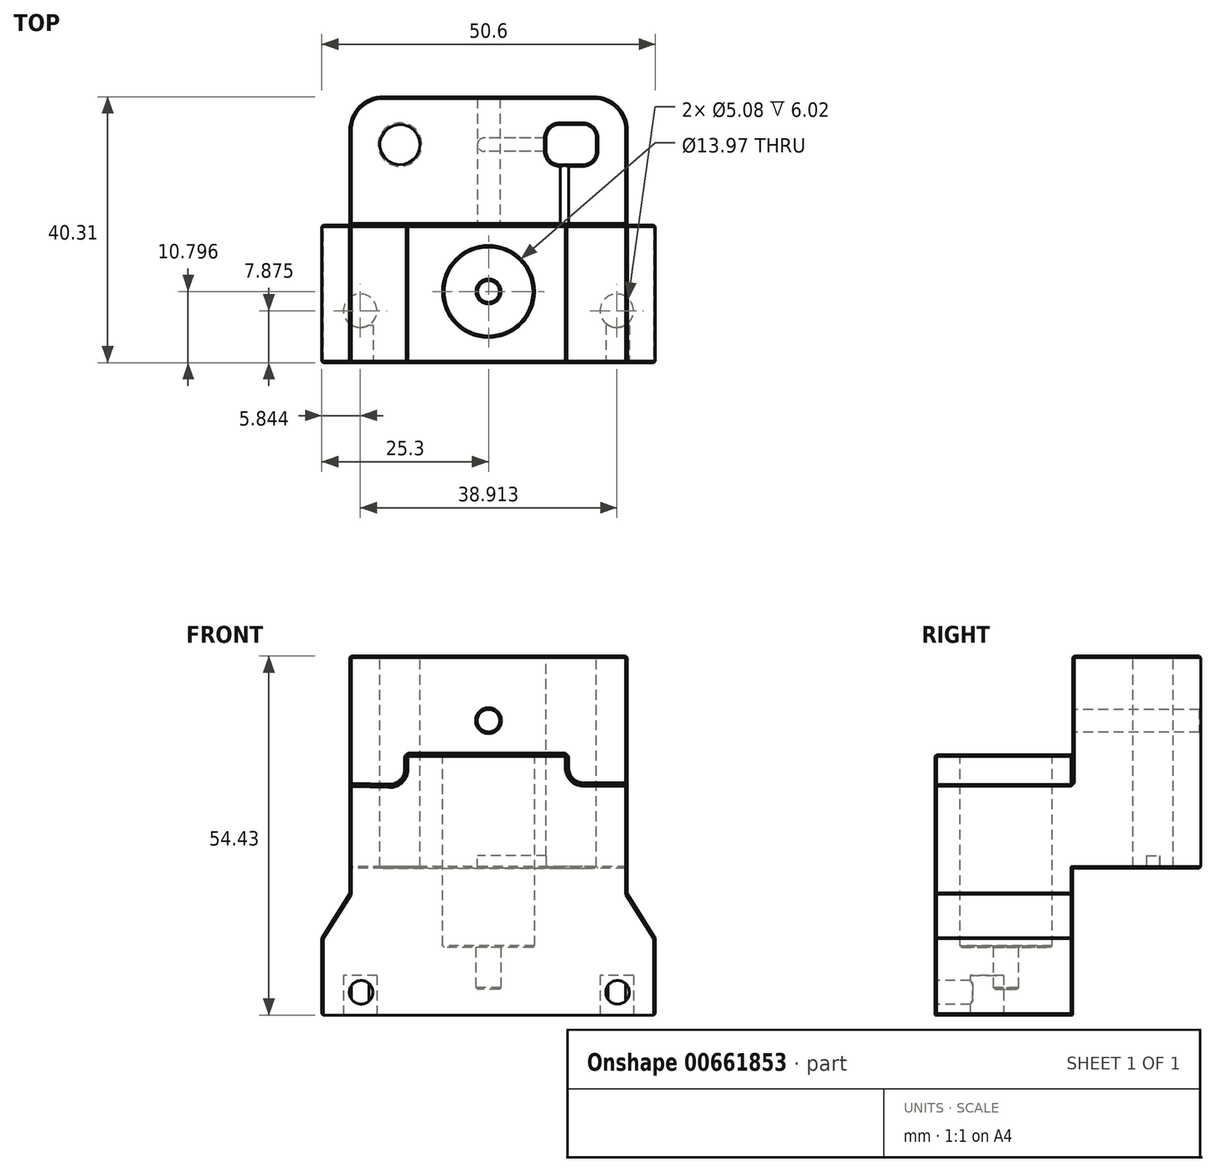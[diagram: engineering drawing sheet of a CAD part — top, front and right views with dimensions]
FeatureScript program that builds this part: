
annotation { "Feature Type Name" : "Feature", "Feature Type Description" : "" }
export const myFeature = defineFeature(function(context is Context, id is Id, definition is map)
    precondition{}
    {
        {
            var Q0;
            Q0=qCreatedBy(makeId("Front.planeOp"),FACE);
            var sketch = newSketch(context, id + "F0", { "sketchPlane" : qUnion([Q0])});
            skLineSegment(sketch, "E0.top", {"start": v(-25.3, -19.99) * mm, "end": v(25.3, -19.99) * mm});
            skPoint(sketch, "E1", {"position": v(-12.47, 14.68) * mm});
            skPoint(sketch, "E2", {"position": v(11.9, 14.96) * mm});
            skPoint(sketch, "E3", {"position": v(-25.3, -8.3) * mm});
            skPoint(sketch, "E4", {"position": v(-21.06, -1.57) * mm});
            skPoint(sketch, "E5", {"position": v(21.06, -1.57) * mm});
            skPoint(sketch, "E6", {"position": v(25.3, -8.3) * mm});
            skLineSegment(sketch, "E7", {"start": v(-25.3, -8.3) * mm, "end": v(-21.06, -1.57) * mm});
            skLineSegment(sketch, "E8", {"start": v(-21.06, -1.57) * mm, "end": v(-21.06, 14.94) * mm});
            skLineSegment(sketch, "E9", {"start": v(-21.06, 14.94) * mm, "end": v(-12.47, 14.68) * mm});
            skLineSegment(sketch, "E10", {"start": v(-12.47, 14.68) * mm, "end": v(-12.47, 19.48) * mm});
            skLineSegment(sketch, "E11", {"start": v(-12.47, 19.48) * mm, "end": v(11.9, 19.48) * mm});
            skLineSegment(sketch, "E12", {"start": v(11.9, 19.48) * mm, "end": v(11.9, 14.96) * mm});
            skLineSegment(sketch, "E13", {"start": v(21.06, 14.96) * mm, "end": v(11.9, 14.96) * mm});
            skLineSegment(sketch, "E14", {"start": v(21.06, 14.96) * mm, "end": v(21.06, -1.57) * mm});
            skLineSegment(sketch, "E15", {"start": v(21.06, -1.57) * mm, "end": v(25.3, -8.3) * mm});
            skLineSegment(sketch, "E16", {"start": v(25.3, -19.99) * mm, "end": v(25.3, -8.3) * mm});
            skLineSegment(sketch, "E17", {"start": v(25.3, -19.99) * mm, "end": v(-25.3, -19.99) * mm});
            skLineSegment(sketch, "E18", {"start": v(-25.3, -19.99) * mm, "end": v(-25.3, -8.3) * mm});
            skSolve(sketch);
        }
        {
            var Q0;
            Q0=makeQuery(id+"F0.imprint","IMPRINT",FACE,{"disambiguationData":[TD([[makeQuery(id+"F0.imprint","IMPRINT",EDGE,{"derivedFrom":sQuery(id+"F0.wireOp",EDGE,"E7")}),-1.0]])]});
            extrude(context, id + "F1", {"entities" : qUnion([Q0]), "depth" : 20.88 * mm, "offsetDistance" : 25.4 * mm});
        }
        {
            var Q0;
            Q0=makeQuery(id+"F1.opExtrude","CAP_FACE",FACE,{"disambiguationData":[OSD([sQuery(id+"F0.wireOp",EDGE,"E7"),sQuery(id+"F0.wireOp",EDGE,"E8"),sQuery(id+"F0.wireOp",EDGE,"E9"),sQuery(id+"F0.wireOp",EDGE,"E10"),sQuery(id+"F0.wireOp",EDGE,"E11"),sQuery(id+"F0.wireOp",EDGE,"E12"),sQuery(id+"F0.wireOp",EDGE,"E13"),sQuery(id+"F0.wireOp",EDGE,"E14"),sQuery(id+"F0.wireOp",EDGE,"E15"),sQuery(id+"F0.wireOp",EDGE,"E16"),sQuery(id+"F0.wireOp",EDGE,"E17"),sQuery(id+"F0.wireOp",EDGE,"E18")])],"isStart":true});
            var sketch = newSketch(context, id + "F2", { "sketchPlane" : qUnion([Q0])});
            skLineSegment(sketch, "E19", {"start": v(-21.06, 2.26) * mm, "end": v(-21.06, 34.44) * mm});
            skLineSegment(sketch, "E20", {"start": v(21.06, 2.26) * mm, "end": v(21.06, 34.44) * mm});
            skLineSegment(sketch, "E21", {"start": v(21.06, 34.44) * mm, "end": v(-21.06, 34.44) * mm});
            skLineSegment(sketch, "E22", {"start": v(-21.06, 2.26) * mm, "end": v(21.06, 2.26) * mm});
            skCircle(sketch, "E23", {"center": v(0, 24.65) * mm, "radius": 1.71 * mm});
            skSolve(sketch);
        }
        {
            var Q0;
            {var subQ0=sQuery(id+"F2.wireOp",EDGE,"E21");Q0=makeQuery(id+"F2.imprint","IMPRINT",FACE,{"disambiguationData":[TD([[makeQuery(id+"F2.imprint","IMPRINT",EDGE,{"derivedFrom":subQ0}),1.0]])]});}
            var Q1;
            {var subQ2=sQuery(id+"F2.wireOp",EDGE,"E22");Q1=makeQuery(id+"F2.imprint","IMPRINT",FACE,{"disambiguationData":[TD([[makeQuery(id+"F2.imprint","IMPRINT",EDGE,{"derivedFrom":subQ2}),1.0]])]});}
            extrude(context, id + "F3", {"entities" : qUnion([Q0, Q1]), "operationType" : NewBodyOperationType.ADD, "depth" : 19.43 * mm, "offsetDistance" : 25.4 * mm});
        }
        {
            var Q0;
            Q0=makeQuery(id+"F3.opExtrude","CAP_FACE",FACE,{"disambiguationData":[OSD([sQuery(id+"F2.wireOp",EDGE,"E19"),sQuery(id+"F2.wireOp",EDGE,"E20"),sQuery(id+"F2.wireOp",EDGE,"E21"),sQuery(id+"F2.wireOp",EDGE,"E22"),sQuery(id+"F2.wireOp",EDGE,"E23")])],"isStart":true});
            var sketch = newSketch(context, id + "F4", { "sketchPlane" : qUnion([Q0])});
            skPoint(sketch, "E24", {"position": v(12.17, 34.44) * mm});
            skPoint(sketch, "E25", {"position": v(10.9, 34.44) * mm});
            skArc(sketch, "E26", {"start": v(10.9, 34.44) * mm, "mid": v(11.53, 34.35) * mm, "end": v(12.17, 34.44) * mm});
            skSolve(sketch);
        }
        {
            var Q0;
            Q0=qCreatedBy(makeId("Front.planeOp"),FACE);
            cPlane(context, id + "F5", {"entities" : qUnion([Q0]), "cplaneType" : CPlaneType.OFFSET, "offset" : 20.88 * mm, "width" : 152.4 * mm, "height" : 152.4 * mm});
        }
        {
            var Q0;
            Q0=qCreatedBy(makeId("Top.planeOp"),FACE);
            cPlane(context, id + "F6", {"entities" : qUnion([Q0]), "cplaneType" : CPlaneType.OFFSET, "offset" : 34.44 * mm, "width" : 152.4 * mm, "height" : 152.4 * mm});
        }
        {
            var Q0;
            Q0=makeQuery(id+"F1.opExtrude","SWEPT_EDGE",EDGE,{"disambiguationData":[OSD([sQuery(id+"F0.wireOp",EDGE,"E12"),sQuery(id+"F0.wireOp",EDGE,"E13")])]});
            var Q1;
            Q1=makeQuery(id+"F1.opExtrude","SWEPT_EDGE",EDGE,{"disambiguationData":[OSD([sQuery(id+"F0.wireOp",EDGE,"E9"),sQuery(id+"F0.wireOp",EDGE,"E10")])]});
            fillet(context, id + "F7", {"entities" : qUnion([Q0, Q1]), "radius" : 2.54 * mm, "tangentPropagation" : true, "allowEdgeOverflow" : false});
        }
        {
            var Q0;
            Q0=makeQuery(id+"F3.opExtrude","CAP_EDGE",EDGE,{"disambiguationData":[OSD([sQuery(id+"F2.wireOp",EDGE,"E19")])],"isStart":false});
            var Q1;
            Q1=makeQuery(id+"F3.opExtrude","CAP_EDGE",EDGE,{"disambiguationData":[OSD([sQuery(id+"F2.wireOp",EDGE,"E20")])],"isStart":false});
            fillet(context, id + "F8", {"entities" : qUnion([Q0, Q1]), "radius" : 5.08 * mm, "tangentPropagation" : true, "allowEdgeOverflow" : false});
        }
        {
            var Q0;
            Q0=qCreatedBy(makeId("Top.planeOp"),FACE);
            cPlane(context, id + "F9", {"entities" : qUnion([Q0]), "cplaneType" : CPlaneType.OFFSET, "offset" : 19.48 * mm, "width" : 152.4 * mm, "height" : 152.4 * mm});
        }
        {
            var Q0;
            Q0=qCreatedBy(id+"F9.planeOp",FACE);
            var sketch = newSketch(context, id + "F10", { "sketchPlane" : qUnion([Q0])});
            skCircle(sketch, "E27", {"center": v(0, -10.08) * mm, "radius": 6.99 * mm});
            skCircle(sketch, "E28", {"center": v(0, -10.08) * mm, "radius": 1.9 * mm});
            skSolve(sketch);
        }
        {
            var Q0;
            Q0 = qSketchRegion(id + "F10", true);
            extrude(context, id + "F11", {"entities" : qUnion([Q0]), "operationType" : NewBodyOperationType.REMOVE, "oppositeDirection" : true, "depth" : 29.2 * mm, "offsetDistance" : 25.4 * mm});
        }
        {
            var Q0;
            Q0=makeQuery(id+"F11.boolean.opBoolean","SPLIT",FACE,{"disambiguationData":[TD([makeQuery(id+"F11.opExtrude","SWEPT_FACE",FACE,{"disambiguationData":[OSD([sQuery(id+"F10.wireOp",EDGE,"E28")])]})])],"derivedFrom":makeQuery(id+"F1.opExtrude","SWEPT_FACE",FACE,{"disambiguationData":[OSD([sQuery(id+"F0.wireOp",EDGE,"E11")])]})});
            extrude(context, id + "F12", {"entities" : qUnion([Q0]), "operationType" : NewBodyOperationType.REMOVE, "oppositeDirection" : true, "depth" : 35.56 * mm, "offsetDistance" : 25.4 * mm});
        }
        {
            var Q0;
            Q0=qCreatedBy(id+"F6.planeOp",FACE);
            var sketch = newSketch(context, id + "F13", { "sketchPlane" : qUnion([Q0])});
            skCircle(sketch, "E29", {"center": v(-13.44, 12.2) * mm, "radius": 3.05 * mm});
            skLineSegment(sketch, "E30.bottom", {"start": v(16.36, 9.14) * mm, "end": v(8.74, 9.14) * mm});
            skLineSegment(sketch, "E30.top", {"start": v(16.36, 15.24) * mm, "end": v(8.74, 15.24) * mm});
            skLineSegment(sketch, "E30.left", {"start": v(16.36, 9.14) * mm, "end": v(16.36, 15.24) * mm});
            skLineSegment(sketch, "E30.right", {"start": v(8.74, 9.14) * mm, "end": v(8.74, 15.24) * mm});
            skSolve(sketch);
        }
        {
            var Q0;
            Q0 = qSketchRegion(id + "F13", true);
            extrude(context, id + "F14", {"entities" : qUnion([Q0]), "operationType" : NewBodyOperationType.REMOVE, "endBound" : BoundingType.THROUGH_ALL, "oppositeDirection" : true, "depth" : 25.4 * mm, "offsetDistance" : 25.4 * mm});
        }
        {
            var Q0;
            Q0=makeQuery(id+"F14.boolean.opBoolean","COPY",EDGE,{"derivedFrom":makeQuery(id+"F14.opExtrude","SWEPT_EDGE",EDGE,{"disambiguationData":[OSD([sQuery(id+"F13.wireOp",EDGE,"E30.bottom"),sQuery(id+"F13.wireOp",EDGE,"E30.left")])]})});
            var Q1;
            Q1=makeQuery(id+"F14.boolean.opBoolean","COPY",EDGE,{"derivedFrom":makeQuery(id+"F14.opExtrude","SWEPT_EDGE",EDGE,{"disambiguationData":[OSD([sQuery(id+"F13.wireOp",EDGE,"E30.top"),sQuery(id+"F13.wireOp",EDGE,"E30.right")])]})});
            var Q2;
            Q2=makeQuery(id+"F14.boolean.opBoolean","COPY",EDGE,{"derivedFrom":makeQuery(id+"F14.opExtrude","SWEPT_EDGE",EDGE,{"disambiguationData":[OSD([sQuery(id+"F13.wireOp",EDGE,"E30.bottom"),sQuery(id+"F13.wireOp",EDGE,"E30.right")])]})});
            var Q3;
            Q3=makeQuery(id+"F14.boolean.opBoolean","COPY",EDGE,{"derivedFrom":makeQuery(id+"F14.opExtrude","SWEPT_EDGE",EDGE,{"disambiguationData":[OSD([sQuery(id+"F13.wireOp",EDGE,"E30.top"),sQuery(id+"F13.wireOp",EDGE,"E30.left")])]})});
            fillet(context, id + "F15", {"entities" : qUnion([Q0, Q1, Q2, Q3]), "radius" : 2.03 * mm, "tangentPropagation" : true, "allowEdgeOverflow" : false});
        }
        {
            var Q0;
            Q0=makeQuery(id+"F8.opFillet","BLEND_EDGE",EDGE,{"blendedFrom":[makeQuery(id+"F3.opExtrude","CAP_EDGE",EDGE,{"disambiguationData":[OSD([sQuery(id+"F2.wireOp",EDGE,"E19")])],"isStart":false}),makeQuery(id+"F3.opExtrude","SWEPT_FACE",FACE,{"disambiguationData":[OSD([sQuery(id+"F2.wireOp",EDGE,"E22")])]})],"blendedInto":[makeQuery(id+"F3.opExtrude","SWEPT_FACE",FACE,{"disambiguationData":[OSD([sQuery(id+"F2.wireOp",EDGE,"E22")])]})]});
            var Q1;
            Q1=makeQuery(id+"F1.opExtrude","SWEPT_EDGE",EDGE,{"disambiguationData":[OSD([sQuery(id+"F0.wireOp",EDGE,"E7"),sQuery(id+"F0.wireOp",EDGE,"E18")])]});
            var Q2;
            {var subQ0=sQuery(id+"F2.wireOp",EDGE,"E19");Q2=makeQuery(id+"F8.opFillet","BLEND_EDGE",EDGE,{"blendedFrom":[makeQuery(id+"F3.opExtrude","CAP_EDGE",EDGE,{"disambiguationData":[OSD([subQ0])],"isStart":false}),makeQuery(id+"F3.opExtrude","CAP_FACE",FACE,{"disambiguationData":[OSD([subQ0,sQuery(id+"F2.wireOp",EDGE,"E20"),sQuery(id+"F2.wireOp",EDGE,"E21"),sQuery(id+"F2.wireOp",EDGE,"E22"),sQuery(id+"F2.wireOp",EDGE,"E23")])],"isStart":false})],"blendedInto":[makeQuery(id+"F3.opExtrude","CAP_FACE",FACE,{"disambiguationData":[OSD([subQ0,sQuery(id+"F2.wireOp",EDGE,"E20"),sQuery(id+"F2.wireOp",EDGE,"E21"),sQuery(id+"F2.wireOp",EDGE,"E22"),sQuery(id+"F2.wireOp",EDGE,"E23")])],"isStart":false})]});}
            var Q3;
            Q3=makeQuery(id+"F8.opFillet","BLEND_EDGE",EDGE,{"blendedFrom":[makeQuery(id+"F3.opExtrude","CAP_EDGE",EDGE,{"disambiguationData":[OSD([sQuery(id+"F2.wireOp",EDGE,"E20")])],"isStart":false}),makeQuery(id+"F3.opExtrude","SWEPT_FACE",FACE,{"disambiguationData":[OSD([sQuery(id+"F2.wireOp",EDGE,"E21")])]})],"blendedInto":[makeQuery(id+"F3.opExtrude","SWEPT_FACE",FACE,{"disambiguationData":[OSD([sQuery(id+"F2.wireOp",EDGE,"E21")])]})]});
            var Q4;
            Q4=makeQuery(id+"F8.opFillet","BLEND_EDGE",EDGE,{"blendedFrom":[makeQuery(id+"F3.opExtrude","CAP_EDGE",EDGE,{"disambiguationData":[OSD([sQuery(id+"F2.wireOp",EDGE,"E19")])],"isStart":false}),makeQuery(id+"F3.opExtrude","SWEPT_FACE",FACE,{"disambiguationData":[OSD([sQuery(id+"F2.wireOp",EDGE,"E21")])]})],"blendedInto":[makeQuery(id+"F3.opExtrude","SWEPT_FACE",FACE,{"disambiguationData":[OSD([sQuery(id+"F2.wireOp",EDGE,"E21")])]})]});
            var Q5;
            Q5=makeQuery(id+"F3.opExtrude","CAP_EDGE",EDGE,{"disambiguationData":[OSD([sQuery(id+"F2.wireOp",EDGE,"E22")])],"isStart":false});
            var Q6;
            Q6=makeQuery(id+"F1.opExtrude","SWEPT_EDGE",EDGE,{"disambiguationData":[OSD([sQuery(id+"F0.wireOp",EDGE,"E17"),sQuery(id+"F0.wireOp",EDGE,"E18")])]});
            var Q7;
            Q7=makeQuery(id+"F1.opExtrude","SWEPT_EDGE",EDGE,{"disambiguationData":[OSD([sQuery(id+"F0.wireOp",EDGE,"E8"),sQuery(id+"F0.wireOp",EDGE,"E9")])]});
            var Q8;
            Q8=makeQuery(id+"F1.opExtrude","SWEPT_EDGE",EDGE,{"disambiguationData":[OSD([sQuery(id+"F0.wireOp",EDGE,"E16"),sQuery(id+"F0.wireOp",EDGE,"E17")])]});
            var Q9;
            Q9=makeQuery(id+"F3.opExtrude","SWEPT_EDGE",EDGE,{"disambiguationData":[OSD([sQuery(id+"F0.wireOp",EDGE,"E8"),sQuery(id+"F2.wireOp",EDGE,"E20"),sQuery(id+"F2.wireOp",EDGE,"E22")])]});
            var Q10;
            Q10=makeQuery(id+"F1.opExtrude","CAP_EDGE",EDGE,{"disambiguationData":[OSD([sQuery(id+"F0.wireOp",EDGE,"E7")])],"isStart":true});
            var Q11;
            Q11=makeQuery(id+"F3.opExtrude","SWEPT_EDGE",EDGE,{"disambiguationData":[OSD([sQuery(id+"F0.wireOp",EDGE,"E14"),sQuery(id+"F2.wireOp",EDGE,"E19"),sQuery(id+"F2.wireOp",EDGE,"E22")])]});
            var Q12;
            Q12=makeQuery(id+"F1.opExtrude","CAP_EDGE",EDGE,{"disambiguationData":[OSD([sQuery(id+"F0.wireOp",EDGE,"E14")])],"isStart":true});
            var Q13;
            Q13=makeQuery(id+"F1.opExtrude","CAP_EDGE",EDGE,{"disambiguationData":[OSD([sQuery(id+"F0.wireOp",EDGE,"E17")])],"isStart":false});
            var Q14;
            Q14=makeQuery(id+"F1.opExtrude","CAP_EDGE",EDGE,{"disambiguationData":[OSD([sQuery(id+"F0.wireOp",EDGE,"E18")])],"isStart":false});
            var Q15;
            Q15=makeQuery(id+"F1.opExtrude","CAP_EDGE",EDGE,{"disambiguationData":[OSD([sQuery(id+"F0.wireOp",EDGE,"E8")])],"isStart":true});
            var Q16;
            Q16=makeQuery(id+"F3.opExtrude","CAP_EDGE",EDGE,{"disambiguationData":[OSD([sQuery(id+"F2.wireOp",EDGE,"E23")])],"isStart":false});
            var Q17;
            Q17=makeQuery(id+"F15.opFillet","BLEND_EDGE",EDGE,{"blendedFrom":[makeQuery(id+"F14.boolean.opBoolean","COPY",EDGE,{"derivedFrom":makeQuery(id+"F14.opExtrude","SWEPT_EDGE",EDGE,{"disambiguationData":[OSD([sQuery(id+"F13.wireOp",EDGE,"E30.top"),sQuery(id+"F13.wireOp",EDGE,"E30.left")])]})}),makeQuery(id+"F3.opExtrude","SWEPT_FACE",FACE,{"disambiguationData":[OSD([sQuery(id+"F2.wireOp",EDGE,"E22")])]})],"blendedInto":[makeQuery(id+"F3.opExtrude","SWEPT_FACE",FACE,{"disambiguationData":[OSD([sQuery(id+"F2.wireOp",EDGE,"E22")])]})]});
            var Q18;
            Q18=makeQuery(id+"F14.boolean.opBoolean","INTERSECT",EDGE,{"derivedFrom":[makeQuery(id+"F3.opExtrude","SWEPT_FACE",FACE,{"disambiguationData":[OSD([sQuery(id+"F2.wireOp",EDGE,"E22")])]}),makeQuery(id+"F14.opExtrude","SWEPT_FACE",FACE,{"disambiguationData":[OSD([sQuery(id+"F13.wireOp",EDGE,"E29")])]})]});
            var Q19;
            Q19=makeQuery(id+"F15.opFillet","BLEND_EDGE",EDGE,{"blendedFrom":[makeQuery(id+"F14.boolean.opBoolean","COPY",EDGE,{"derivedFrom":makeQuery(id+"F14.opExtrude","SWEPT_EDGE",EDGE,{"disambiguationData":[OSD([sQuery(id+"F13.wireOp",EDGE,"E30.top"),sQuery(id+"F13.wireOp",EDGE,"E30.right")])]})}),makeQuery(id+"F3.opExtrude","SWEPT_FACE",FACE,{"disambiguationData":[OSD([sQuery(id+"F2.wireOp",EDGE,"E22")])]})],"blendedInto":[makeQuery(id+"F3.opExtrude","SWEPT_FACE",FACE,{"disambiguationData":[OSD([sQuery(id+"F2.wireOp",EDGE,"E22")])]})]});
            var Q20;
            Q20=makeQuery(id+"F3.opExtrude","CAP_EDGE",EDGE,{"disambiguationData":[OSD([sQuery(id+"F2.wireOp",EDGE,"E21")])],"isStart":false});
            var Q21;
            Q21=makeQuery(id+"F8.opFillet","BLEND_EDGE",EDGE,{"blendedFrom":[makeQuery(id+"F3.opExtrude","CAP_EDGE",EDGE,{"disambiguationData":[OSD([sQuery(id+"F2.wireOp",EDGE,"E20")])],"isStart":false}),makeQuery(id+"F3.opExtrude","SWEPT_FACE",FACE,{"disambiguationData":[OSD([sQuery(id+"F2.wireOp",EDGE,"E22")])]})],"blendedInto":[makeQuery(id+"F3.opExtrude","SWEPT_FACE",FACE,{"disambiguationData":[OSD([sQuery(id+"F2.wireOp",EDGE,"E22")])]})]});
            var Q22;
            {var subQ0=sQuery(id+"F2.wireOp",EDGE,"E20");Q22=makeQuery(id+"F8.opFillet","BLEND_EDGE",EDGE,{"blendedFrom":[makeQuery(id+"F3.opExtrude","CAP_EDGE",EDGE,{"disambiguationData":[OSD([subQ0])],"isStart":false}),makeQuery(id+"F3.boolean.opBoolean","MERGE",FACE,{"derivedFrom":[makeQuery(id+"F1.opExtrude","SWEPT_FACE",FACE,{"disambiguationData":[OSD([sQuery(id+"F0.wireOp",EDGE,"E8")])]}),makeQuery(id+"F3.opExtrude","SWEPT_FACE",FACE,{"disambiguationData":[OSD([subQ0])]})]})],"blendedInto":[makeQuery(id+"F3.boolean.opBoolean","MERGE",FACE,{"derivedFrom":[makeQuery(id+"F1.opExtrude","SWEPT_FACE",FACE,{"disambiguationData":[OSD([sQuery(id+"F0.wireOp",EDGE,"E8")])]}),makeQuery(id+"F3.opExtrude","SWEPT_FACE",FACE,{"disambiguationData":[OSD([subQ0])]})]})]});}
            var Q23;
            Q23=makeQuery(id+"F3.opExtrude","CAP_EDGE",EDGE,{"disambiguationData":[OSD([sQuery(id+"F2.wireOp",EDGE,"E20")])],"isStart":true});
            var Q24;
            Q24=makeQuery(id+"F1.opExtrude","SWEPT_EDGE",EDGE,{"disambiguationData":[OSD([sQuery(id+"F0.wireOp",EDGE,"E15"),sQuery(id+"F0.wireOp",EDGE,"E16")])]});
            var Q25;
            Q25=makeQuery(id+"F1.opExtrude","SWEPT_EDGE",EDGE,{"disambiguationData":[OSD([sQuery(id+"F0.wireOp",EDGE,"E7"),sQuery(id+"F0.wireOp",EDGE,"E8")])]});
            var Q26;
            Q26=makeQuery(id+"F1.opExtrude","CAP_EDGE",EDGE,{"disambiguationData":[OSD([sQuery(id+"F0.wireOp",EDGE,"E9")])],"isStart":true});
            var Q27;
            Q27=makeQuery(id+"F1.opExtrude","CAP_EDGE",EDGE,{"disambiguationData":[OSD([sQuery(id+"F0.wireOp",EDGE,"E11")])],"isStart":true});
            var Q28;
            Q28=makeQuery(id+"F1.opExtrude","CAP_EDGE",EDGE,{"disambiguationData":[OSD([sQuery(id+"F0.wireOp",EDGE,"E16")])],"isStart":false});
            var Q29;
            Q29=makeQuery(id+"F1.opExtrude","SWEPT_EDGE",EDGE,{"disambiguationData":[OSD([sQuery(id+"F0.wireOp",EDGE,"E13"),sQuery(id+"F0.wireOp",EDGE,"E14")])]});
            var Q30;
            Q30=makeQuery(id+"F1.opExtrude","CAP_EDGE",EDGE,{"disambiguationData":[OSD([sQuery(id+"F0.wireOp",EDGE,"E14")])],"isStart":false});
            var Q31;
            Q31=makeQuery(id+"F1.opExtrude","CAP_EDGE",EDGE,{"disambiguationData":[OSD([sQuery(id+"F0.wireOp",EDGE,"E7")])],"isStart":false});
            var Q32;
            Q32=makeQuery(id+"F3.opExtrude","SWEPT_EDGE",EDGE,{"disambiguationData":[OSD([sQuery(id+"F2.wireOp",EDGE,"E19"),sQuery(id+"F2.wireOp",EDGE,"E21")])]});
            var Q33;
            Q33=makeQuery(id+"F1.opExtrude","SWEPT_EDGE",EDGE,{"disambiguationData":[OSD([sQuery(id+"F0.wireOp",EDGE,"E14"),sQuery(id+"F0.wireOp",EDGE,"E15")])]});
            var Q34;
            {var subQ0=sQuery(id+"F0.wireOp",EDGE,"E13");Q34=makeQuery(id+"F7.opFillet","BLEND_EDGE",EDGE,{"blendedFrom":[makeQuery(id+"F1.opExtrude","SWEPT_EDGE",EDGE,{"disambiguationData":[OSD([sQuery(id+"F0.wireOp",EDGE,"E12"),subQ0])]}),makeQuery(id+"F1.opExtrude","SWEPT_FACE",FACE,{"disambiguationData":[OSD([subQ0])]})],"blendedInto":[makeQuery(id+"F1.opExtrude","SWEPT_FACE",FACE,{"disambiguationData":[OSD([subQ0])]})]});}
            var Q35;
            Q35=makeQuery(id+"F3.opExtrude","SWEPT_EDGE",EDGE,{"disambiguationData":[OSD([sQuery(id+"F2.wireOp",EDGE,"E20"),sQuery(id+"F2.wireOp",EDGE,"E21")])]});
            var Q36;
            Q36=makeQuery(id+"F1.opExtrude","CAP_EDGE",EDGE,{"disambiguationData":[OSD([sQuery(id+"F0.wireOp",EDGE,"E16")])],"isStart":true});
            var Q37;
            Q37=makeQuery(id+"F1.opExtrude","SWEPT_EDGE",EDGE,{"disambiguationData":[OSD([sQuery(id+"F0.wireOp",EDGE,"E11"),sQuery(id+"F0.wireOp",EDGE,"E12")])]});
            var Q38;
            Q38=makeQuery(id+"F1.opExtrude","CAP_EDGE",EDGE,{"disambiguationData":[OSD([sQuery(id+"F0.wireOp",EDGE,"E8")])],"isStart":false});
            var Q39;
            Q39=makeQuery(id+"F1.opExtrude","CAP_EDGE",EDGE,{"disambiguationData":[OSD([sQuery(id+"F0.wireOp",EDGE,"E11")])],"isStart":false});
            var Q40;
            Q40=makeQuery(id+"F1.opExtrude","CAP_EDGE",EDGE,{"disambiguationData":[OSD([sQuery(id+"F0.wireOp",EDGE,"E18")])],"isStart":true});
            var Q41;
            {var subQ0=sQuery(id+"F0.wireOp",EDGE,"E10");var subQ1=sQuery(id+"F0.wireOp",EDGE,"E9");Q41=makeQuery(id+"F7.opFillet","BLEND_EDGE",EDGE,{"blendedFrom":[makeQuery(id+"F1.opExtrude","SWEPT_EDGE",EDGE,{"disambiguationData":[OSD([subQ1,subQ0])]}),makeQuery(id+"F1.opExtrude","CAP_FACE",FACE,{"disambiguationData":[OSD([sQuery(id+"F0.wireOp",EDGE,"E7"),sQuery(id+"F0.wireOp",EDGE,"E8"),subQ1,subQ0,sQuery(id+"F0.wireOp",EDGE,"E11"),sQuery(id+"F0.wireOp",EDGE,"E12"),sQuery(id+"F0.wireOp",EDGE,"E13"),sQuery(id+"F0.wireOp",EDGE,"E14"),sQuery(id+"F0.wireOp",EDGE,"E15"),sQuery(id+"F0.wireOp",EDGE,"E16"),sQuery(id+"F0.wireOp",EDGE,"E17"),sQuery(id+"F0.wireOp",EDGE,"E18")])],"isStart":false})],"blendedInto":[makeQuery(id+"F1.opExtrude","CAP_FACE",FACE,{"disambiguationData":[OSD([sQuery(id+"F0.wireOp",EDGE,"E7"),sQuery(id+"F0.wireOp",EDGE,"E8"),subQ1,subQ0,sQuery(id+"F0.wireOp",EDGE,"E11"),sQuery(id+"F0.wireOp",EDGE,"E12"),sQuery(id+"F0.wireOp",EDGE,"E13"),sQuery(id+"F0.wireOp",EDGE,"E14"),sQuery(id+"F0.wireOp",EDGE,"E15"),sQuery(id+"F0.wireOp",EDGE,"E16"),sQuery(id+"F0.wireOp",EDGE,"E17"),sQuery(id+"F0.wireOp",EDGE,"E18")])],"isStart":false})]});}
            var Q42;
            Q42=makeQuery(id+"F1.opExtrude","CAP_EDGE",EDGE,{"disambiguationData":[OSD([sQuery(id+"F0.wireOp",EDGE,"E15")])],"isStart":false});
            var Q43;
            Q43=makeQuery(id+"F7.opFillet","BLEND_EDGE",EDGE,{"blendedFrom":[makeQuery(id+"F1.opExtrude","SWEPT_EDGE",EDGE,{"disambiguationData":[OSD([sQuery(id+"F0.wireOp",EDGE,"E9"),sQuery(id+"F0.wireOp",EDGE,"E10")])]}),makeQuery(id+"F3.opExtrude","CAP_FACE",FACE,{"disambiguationData":[OSD([sQuery(id+"F2.wireOp",EDGE,"E19"),sQuery(id+"F2.wireOp",EDGE,"E20"),sQuery(id+"F2.wireOp",EDGE,"E21"),sQuery(id+"F2.wireOp",EDGE,"E22"),sQuery(id+"F2.wireOp",EDGE,"E23")])],"isStart":true})],"blendedInto":[makeQuery(id+"F3.opExtrude","CAP_FACE",FACE,{"disambiguationData":[OSD([sQuery(id+"F2.wireOp",EDGE,"E19"),sQuery(id+"F2.wireOp",EDGE,"E20"),sQuery(id+"F2.wireOp",EDGE,"E21"),sQuery(id+"F2.wireOp",EDGE,"E22"),sQuery(id+"F2.wireOp",EDGE,"E23")])],"isStart":true})]});
            var Q44;
            Q44=makeQuery(id+"F1.opExtrude","CAP_EDGE",EDGE,{"disambiguationData":[OSD([sQuery(id+"F0.wireOp",EDGE,"E17")])],"isStart":true});
            var Q45;
            {var subQ0=sQuery(id+"F0.wireOp",EDGE,"E13");var subQ1=sQuery(id+"F0.wireOp",EDGE,"E12");Q45=makeQuery(id+"F7.opFillet","BLEND_EDGE",EDGE,{"blendedFrom":[makeQuery(id+"F1.opExtrude","SWEPT_EDGE",EDGE,{"disambiguationData":[OSD([subQ1,subQ0])]}),makeQuery(id+"F1.opExtrude","CAP_FACE",FACE,{"disambiguationData":[OSD([sQuery(id+"F0.wireOp",EDGE,"E7"),sQuery(id+"F0.wireOp",EDGE,"E8"),sQuery(id+"F0.wireOp",EDGE,"E9"),sQuery(id+"F0.wireOp",EDGE,"E10"),sQuery(id+"F0.wireOp",EDGE,"E11"),subQ1,subQ0,sQuery(id+"F0.wireOp",EDGE,"E14"),sQuery(id+"F0.wireOp",EDGE,"E15"),sQuery(id+"F0.wireOp",EDGE,"E16"),sQuery(id+"F0.wireOp",EDGE,"E17"),sQuery(id+"F0.wireOp",EDGE,"E18")])],"isStart":false})],"blendedInto":[makeQuery(id+"F1.opExtrude","CAP_FACE",FACE,{"disambiguationData":[OSD([sQuery(id+"F0.wireOp",EDGE,"E7"),sQuery(id+"F0.wireOp",EDGE,"E8"),sQuery(id+"F0.wireOp",EDGE,"E9"),sQuery(id+"F0.wireOp",EDGE,"E10"),sQuery(id+"F0.wireOp",EDGE,"E11"),subQ1,subQ0,sQuery(id+"F0.wireOp",EDGE,"E14"),sQuery(id+"F0.wireOp",EDGE,"E15"),sQuery(id+"F0.wireOp",EDGE,"E16"),sQuery(id+"F0.wireOp",EDGE,"E17"),sQuery(id+"F0.wireOp",EDGE,"E18")])],"isStart":false})]});}
            var Q46;
            Q46=makeQuery(id+"F12.boolean.opBoolean","COPY",EDGE,{"derivedFrom":makeQuery(id+"F12.opExtrude","CAP_EDGE",EDGE,{"disambiguationData":[OSD([sQuery(id+"F10.wireOp",EDGE,"E28")])],"isStart":false})});
            var Q47;
            Q47=makeQuery(id+"F3.opExtrude","CAP_EDGE",EDGE,{"disambiguationData":[OSD([sQuery(id+"F2.wireOp",EDGE,"E22")])],"isStart":true});
            var Q48;
            Q48=makeQuery(id+"F1.opExtrude","CAP_EDGE",EDGE,{"disambiguationData":[OSD([sQuery(id+"F0.wireOp",EDGE,"E15")])],"isStart":true});
            var Q49;
            Q49=makeQuery(id+"F3.opExtrude","CAP_EDGE",EDGE,{"disambiguationData":[OSD([sQuery(id+"F2.wireOp",EDGE,"E19")])],"isStart":true});
            var Q50;
            {var subQ0=sQuery(id+"F0.wireOp",EDGE,"E9");Q50=makeQuery(id+"F7.opFillet","BLEND_EDGE",EDGE,{"blendedFrom":[makeQuery(id+"F1.opExtrude","SWEPT_EDGE",EDGE,{"disambiguationData":[OSD([subQ0,sQuery(id+"F0.wireOp",EDGE,"E10")])]}),makeQuery(id+"F1.opExtrude","SWEPT_FACE",FACE,{"disambiguationData":[OSD([subQ0])]})],"blendedInto":[makeQuery(id+"F1.opExtrude","SWEPT_FACE",FACE,{"disambiguationData":[OSD([subQ0])]})]});}
            var Q51;
            Q51=makeQuery(id+"F14.boolean.opBoolean","INTERSECT",EDGE,{"derivedFrom":[makeQuery(id+"F3.opExtrude","SWEPT_FACE",FACE,{"disambiguationData":[OSD([sQuery(id+"F2.wireOp",EDGE,"E22")])]}),makeQuery(id+"F14.opExtrude","SWEPT_FACE",FACE,{"disambiguationData":[OSD([sQuery(id+"F13.wireOp",EDGE,"E30.top")])]})]});
            var Q52;
            Q52=makeQuery(id+"F14.boolean.opBoolean","INTERSECT",EDGE,{"derivedFrom":[makeQuery(id+"F3.opExtrude","SWEPT_FACE",FACE,{"disambiguationData":[OSD([sQuery(id+"F2.wireOp",EDGE,"E22")])]}),makeQuery(id+"F14.opExtrude","SWEPT_FACE",FACE,{"disambiguationData":[OSD([sQuery(id+"F13.wireOp",EDGE,"E30.bottom")])]})]});
            var Q53;
            Q53=makeQuery(id+"F14.boolean.opBoolean","COPY",EDGE,{"derivedFrom":makeQuery(id+"F14.opExtrude","CAP_EDGE",EDGE,{"disambiguationData":[OSD([sQuery(id+"F13.wireOp",EDGE,"E30.top")])],"isStart":true})});
            var Q54;
            Q54=makeQuery(id+"F14.boolean.opBoolean","COPY",EDGE,{"derivedFrom":makeQuery(id+"F14.opExtrude","CAP_EDGE",EDGE,{"disambiguationData":[OSD([sQuery(id+"F13.wireOp",EDGE,"E30.bottom")])],"isStart":true})});
            var Q55;
            {var subQ0=sQuery(id+"F13.wireOp",EDGE,"E30.top");Q55=makeQuery(id+"F15.opFillet","BLEND_EDGE",EDGE,{"blendedFrom":[makeQuery(id+"F14.boolean.opBoolean","COPY",EDGE,{"derivedFrom":makeQuery(id+"F14.opExtrude","SWEPT_EDGE",EDGE,{"disambiguationData":[OSD([subQ0,sQuery(id+"F13.wireOp",EDGE,"E30.right")])]})}),makeQuery(id+"F14.boolean.opBoolean","COPY",FACE,{"derivedFrom":makeQuery(id+"F14.opExtrude","SWEPT_FACE",FACE,{"disambiguationData":[OSD([subQ0])]})})],"blendedInto":[makeQuery(id+"F14.boolean.opBoolean","COPY",FACE,{"derivedFrom":makeQuery(id+"F14.opExtrude","SWEPT_FACE",FACE,{"disambiguationData":[OSD([subQ0])]})})]});}
            var Q56;
            Q56=makeQuery(id+"F15.opFillet","BLEND_EDGE",EDGE,{"blendedFrom":[makeQuery(id+"F14.boolean.opBoolean","COPY",EDGE,{"derivedFrom":makeQuery(id+"F14.opExtrude","SWEPT_EDGE",EDGE,{"disambiguationData":[OSD([sQuery(id+"F13.wireOp",EDGE,"E30.top"),sQuery(id+"F13.wireOp",EDGE,"E30.left")])]})}),makeQuery(id+"F3.opExtrude","SWEPT_FACE",FACE,{"disambiguationData":[OSD([sQuery(id+"F2.wireOp",EDGE,"E21")])]})],"blendedInto":[makeQuery(id+"F3.opExtrude","SWEPT_FACE",FACE,{"disambiguationData":[OSD([sQuery(id+"F2.wireOp",EDGE,"E21")])]})]});
            var Q57;
            {var subQ0=sQuery(id+"F13.wireOp",EDGE,"E30.left");Q57=makeQuery(id+"F15.opFillet","BLEND_EDGE",EDGE,{"blendedFrom":[makeQuery(id+"F14.boolean.opBoolean","COPY",EDGE,{"derivedFrom":makeQuery(id+"F14.opExtrude","SWEPT_EDGE",EDGE,{"disambiguationData":[OSD([sQuery(id+"F13.wireOp",EDGE,"E30.top"),subQ0])]})}),makeQuery(id+"F14.boolean.opBoolean","COPY",FACE,{"derivedFrom":makeQuery(id+"F14.opExtrude","SWEPT_FACE",FACE,{"disambiguationData":[OSD([subQ0])]})})],"blendedInto":[makeQuery(id+"F14.boolean.opBoolean","COPY",FACE,{"derivedFrom":makeQuery(id+"F14.opExtrude","SWEPT_FACE",FACE,{"disambiguationData":[OSD([subQ0])]})})]});}
            var Q58;
            {var subQ0=sQuery(id+"F13.wireOp",EDGE,"E30.top");Q58=makeQuery(id+"F15.opFillet","BLEND_EDGE",EDGE,{"blendedFrom":[makeQuery(id+"F14.boolean.opBoolean","COPY",EDGE,{"derivedFrom":makeQuery(id+"F14.opExtrude","SWEPT_EDGE",EDGE,{"disambiguationData":[OSD([subQ0,sQuery(id+"F13.wireOp",EDGE,"E30.left")])]})}),makeQuery(id+"F14.boolean.opBoolean","COPY",FACE,{"derivedFrom":makeQuery(id+"F14.opExtrude","SWEPT_FACE",FACE,{"disambiguationData":[OSD([subQ0])]})})],"blendedInto":[makeQuery(id+"F14.boolean.opBoolean","COPY",FACE,{"derivedFrom":makeQuery(id+"F14.opExtrude","SWEPT_FACE",FACE,{"disambiguationData":[OSD([subQ0])]})})]});}
            var Q59;
            Q59=makeQuery(id+"F15.opFillet","BLEND_EDGE",EDGE,{"blendedFrom":[makeQuery(id+"F14.boolean.opBoolean","COPY",EDGE,{"derivedFrom":makeQuery(id+"F14.opExtrude","SWEPT_EDGE",EDGE,{"disambiguationData":[OSD([sQuery(id+"F13.wireOp",EDGE,"E30.bottom"),sQuery(id+"F13.wireOp",EDGE,"E30.right")])]})}),makeQuery(id+"F3.opExtrude","SWEPT_FACE",FACE,{"disambiguationData":[OSD([sQuery(id+"F2.wireOp",EDGE,"E22")])]})],"blendedInto":[makeQuery(id+"F3.opExtrude","SWEPT_FACE",FACE,{"disambiguationData":[OSD([sQuery(id+"F2.wireOp",EDGE,"E22")])]})]});
            var Q60;
            {var subQ0=sQuery(id+"F13.wireOp",EDGE,"E30.right");Q60=makeQuery(id+"F15.opFillet","BLEND_EDGE",EDGE,{"blendedFrom":[makeQuery(id+"F14.boolean.opBoolean","COPY",EDGE,{"derivedFrom":makeQuery(id+"F14.opExtrude","SWEPT_EDGE",EDGE,{"disambiguationData":[OSD([sQuery(id+"F13.wireOp",EDGE,"E30.top"),subQ0])]})}),makeQuery(id+"F14.boolean.opBoolean","COPY",FACE,{"derivedFrom":makeQuery(id+"F14.opExtrude","SWEPT_FACE",FACE,{"disambiguationData":[OSD([subQ0])]})})],"blendedInto":[makeQuery(id+"F14.boolean.opBoolean","COPY",FACE,{"derivedFrom":makeQuery(id+"F14.opExtrude","SWEPT_FACE",FACE,{"disambiguationData":[OSD([subQ0])]})})]});}
            var Q61;
            Q61=makeQuery(id+"F15.opFillet","BLEND_EDGE",EDGE,{"blendedFrom":[makeQuery(id+"F14.boolean.opBoolean","COPY",EDGE,{"derivedFrom":makeQuery(id+"F14.opExtrude","SWEPT_EDGE",EDGE,{"disambiguationData":[OSD([sQuery(id+"F13.wireOp",EDGE,"E30.top"),sQuery(id+"F13.wireOp",EDGE,"E30.right")])]})}),makeQuery(id+"F3.opExtrude","SWEPT_FACE",FACE,{"disambiguationData":[OSD([sQuery(id+"F2.wireOp",EDGE,"E21")])]})],"blendedInto":[makeQuery(id+"F3.opExtrude","SWEPT_FACE",FACE,{"disambiguationData":[OSD([sQuery(id+"F2.wireOp",EDGE,"E21")])]})]});
            var Q62;
            {var subQ0=sQuery(id+"F13.wireOp",EDGE,"E30.bottom");Q62=makeQuery(id+"F15.opFillet","BLEND_EDGE",EDGE,{"blendedFrom":[makeQuery(id+"F14.boolean.opBoolean","COPY",EDGE,{"derivedFrom":makeQuery(id+"F14.opExtrude","SWEPT_EDGE",EDGE,{"disambiguationData":[OSD([subQ0,sQuery(id+"F13.wireOp",EDGE,"E30.left")])]})}),makeQuery(id+"F14.boolean.opBoolean","COPY",FACE,{"derivedFrom":makeQuery(id+"F14.opExtrude","SWEPT_FACE",FACE,{"disambiguationData":[OSD([subQ0])]})})],"blendedInto":[makeQuery(id+"F14.boolean.opBoolean","COPY",FACE,{"derivedFrom":makeQuery(id+"F14.opExtrude","SWEPT_FACE",FACE,{"disambiguationData":[OSD([subQ0])]})})]});}
            var Q63;
            {var subQ0=sQuery(id+"F13.wireOp",EDGE,"E30.left");Q63=makeQuery(id+"F15.opFillet","BLEND_EDGE",EDGE,{"blendedFrom":[makeQuery(id+"F14.boolean.opBoolean","COPY",EDGE,{"derivedFrom":makeQuery(id+"F14.opExtrude","SWEPT_EDGE",EDGE,{"disambiguationData":[OSD([sQuery(id+"F13.wireOp",EDGE,"E30.bottom"),subQ0])]})}),makeQuery(id+"F14.boolean.opBoolean","COPY",FACE,{"derivedFrom":makeQuery(id+"F14.opExtrude","SWEPT_FACE",FACE,{"disambiguationData":[OSD([subQ0])]})})],"blendedInto":[makeQuery(id+"F14.boolean.opBoolean","COPY",FACE,{"derivedFrom":makeQuery(id+"F14.opExtrude","SWEPT_FACE",FACE,{"disambiguationData":[OSD([subQ0])]})})]});}
            var Q64;
            Q64=makeQuery(id+"F14.boolean.opBoolean","COPY",EDGE,{"derivedFrom":makeQuery(id+"F14.opExtrude","CAP_EDGE",EDGE,{"disambiguationData":[OSD([sQuery(id+"F13.wireOp",EDGE,"E29")])],"isStart":true})});
            var Q65;
            Q65=makeQuery(id+"F15.opFillet","BLEND_EDGE",EDGE,{"blendedFrom":[makeQuery(id+"F14.boolean.opBoolean","COPY",EDGE,{"derivedFrom":makeQuery(id+"F14.opExtrude","SWEPT_EDGE",EDGE,{"disambiguationData":[OSD([sQuery(id+"F13.wireOp",EDGE,"E30.bottom"),sQuery(id+"F13.wireOp",EDGE,"E30.left")])]})}),makeQuery(id+"F3.opExtrude","SWEPT_FACE",FACE,{"disambiguationData":[OSD([sQuery(id+"F2.wireOp",EDGE,"E22")])]})],"blendedInto":[makeQuery(id+"F3.opExtrude","SWEPT_FACE",FACE,{"disambiguationData":[OSD([sQuery(id+"F2.wireOp",EDGE,"E22")])]})]});
            var Q66;
            {var subQ0=sQuery(id+"F13.wireOp",EDGE,"E30.bottom");Q66=makeQuery(id+"F15.opFillet","BLEND_EDGE",EDGE,{"blendedFrom":[makeQuery(id+"F14.boolean.opBoolean","COPY",EDGE,{"derivedFrom":makeQuery(id+"F14.opExtrude","SWEPT_EDGE",EDGE,{"disambiguationData":[OSD([subQ0,sQuery(id+"F13.wireOp",EDGE,"E30.right")])]})}),makeQuery(id+"F14.boolean.opBoolean","COPY",FACE,{"derivedFrom":makeQuery(id+"F14.opExtrude","SWEPT_FACE",FACE,{"disambiguationData":[OSD([subQ0])]})})],"blendedInto":[makeQuery(id+"F14.boolean.opBoolean","COPY",FACE,{"derivedFrom":makeQuery(id+"F14.opExtrude","SWEPT_FACE",FACE,{"disambiguationData":[OSD([subQ0])]})})]});}
            var Q67;
            {var subQ0=sQuery(id+"F13.wireOp",EDGE,"E30.right");Q67=makeQuery(id+"F15.opFillet","BLEND_EDGE",EDGE,{"blendedFrom":[makeQuery(id+"F14.boolean.opBoolean","COPY",EDGE,{"derivedFrom":makeQuery(id+"F14.opExtrude","SWEPT_EDGE",EDGE,{"disambiguationData":[OSD([sQuery(id+"F13.wireOp",EDGE,"E30.bottom"),subQ0])]})}),makeQuery(id+"F14.boolean.opBoolean","COPY",FACE,{"derivedFrom":makeQuery(id+"F14.opExtrude","SWEPT_FACE",FACE,{"disambiguationData":[OSD([subQ0])]})})],"blendedInto":[makeQuery(id+"F14.boolean.opBoolean","COPY",FACE,{"derivedFrom":makeQuery(id+"F14.opExtrude","SWEPT_FACE",FACE,{"disambiguationData":[OSD([subQ0])]})})]});}
            var Q68;
            Q68=makeQuery(id+"F3.opExtrude","CAP_EDGE",EDGE,{"disambiguationData":[OSD([sQuery(id+"F2.wireOp",EDGE,"E21")])],"isStart":true});
            var Q69;
            {var subQ0=sQuery(id+"F2.wireOp",EDGE,"E20");Q69=makeQuery(id+"F8.opFillet","BLEND_EDGE",EDGE,{"blendedFrom":[makeQuery(id+"F3.opExtrude","CAP_EDGE",EDGE,{"disambiguationData":[OSD([subQ0])],"isStart":false}),makeQuery(id+"F3.opExtrude","CAP_FACE",FACE,{"disambiguationData":[OSD([sQuery(id+"F2.wireOp",EDGE,"E19"),subQ0,sQuery(id+"F2.wireOp",EDGE,"E21"),sQuery(id+"F2.wireOp",EDGE,"E22"),sQuery(id+"F2.wireOp",EDGE,"E23")])],"isStart":false})],"blendedInto":[makeQuery(id+"F3.opExtrude","CAP_FACE",FACE,{"disambiguationData":[OSD([sQuery(id+"F2.wireOp",EDGE,"E19"),subQ0,sQuery(id+"F2.wireOp",EDGE,"E21"),sQuery(id+"F2.wireOp",EDGE,"E22"),sQuery(id+"F2.wireOp",EDGE,"E23")])],"isStart":false})]});}
            var Q70;
            {var subQ0=sQuery(id+"F2.wireOp",EDGE,"E19");Q70=makeQuery(id+"F8.opFillet","BLEND_EDGE",EDGE,{"blendedFrom":[makeQuery(id+"F3.opExtrude","CAP_EDGE",EDGE,{"disambiguationData":[OSD([subQ0])],"isStart":false}),makeQuery(id+"F3.boolean.opBoolean","MERGE",FACE,{"derivedFrom":[makeQuery(id+"F1.opExtrude","SWEPT_FACE",FACE,{"disambiguationData":[OSD([sQuery(id+"F0.wireOp",EDGE,"E14")])]}),makeQuery(id+"F3.opExtrude","SWEPT_FACE",FACE,{"disambiguationData":[OSD([subQ0])]})]})],"blendedInto":[makeQuery(id+"F3.boolean.opBoolean","MERGE",FACE,{"derivedFrom":[makeQuery(id+"F1.opExtrude","SWEPT_FACE",FACE,{"disambiguationData":[OSD([sQuery(id+"F0.wireOp",EDGE,"E14")])]}),makeQuery(id+"F3.opExtrude","SWEPT_FACE",FACE,{"disambiguationData":[OSD([subQ0])]})]})]});}
            var Q71;
            Q71=makeQuery(id+"F11.boolean.opBoolean","COPY",EDGE,{"derivedFrom":makeQuery(id+"F11.opExtrude","CAP_EDGE",EDGE,{"disambiguationData":[OSD([sQuery(id+"F10.wireOp",EDGE,"E27")])],"isStart":true})});
            var Q72;
            Q72=makeQuery(id+"F11.boolean.opBoolean","COPY",EDGE,{"derivedFrom":makeQuery(id+"F11.opExtrude","CAP_EDGE",EDGE,{"disambiguationData":[OSD([sQuery(id+"F10.wireOp",EDGE,"E27")])],"isStart":false})});
            var Q73;
            Q73=makeQuery(id+"F3.opExtrude","CAP_EDGE",EDGE,{"disambiguationData":[OSD([sQuery(id+"F2.wireOp",EDGE,"E23")])],"isStart":true});
            var Q74;
            Q74=makeQuery(id+"F1.opExtrude","SWEPT_EDGE",EDGE,{"disambiguationData":[OSD([sQuery(id+"F0.wireOp",EDGE,"E10"),sQuery(id+"F0.wireOp",EDGE,"E11")])]});
            var Q75;
            Q75=makeQuery(id+"F1.opExtrude","CAP_EDGE",EDGE,{"disambiguationData":[OSD([sQuery(id+"F0.wireOp",EDGE,"E9")])],"isStart":false});
            var Q76;
            Q76=makeQuery(id+"F1.opExtrude","CAP_EDGE",EDGE,{"disambiguationData":[OSD([sQuery(id+"F0.wireOp",EDGE,"E10")])],"isStart":true});
            var Q77;
            Q77=makeQuery(id+"F7.opFillet","BLEND_EDGE",EDGE,{"blendedFrom":[makeQuery(id+"F1.opExtrude","SWEPT_EDGE",EDGE,{"disambiguationData":[OSD([sQuery(id+"F0.wireOp",EDGE,"E12"),sQuery(id+"F0.wireOp",EDGE,"E13")])]}),makeQuery(id+"F3.opExtrude","CAP_FACE",FACE,{"disambiguationData":[OSD([sQuery(id+"F2.wireOp",EDGE,"E19"),sQuery(id+"F2.wireOp",EDGE,"E20"),sQuery(id+"F2.wireOp",EDGE,"E21"),sQuery(id+"F2.wireOp",EDGE,"E22"),sQuery(id+"F2.wireOp",EDGE,"E23")])],"isStart":true})],"blendedInto":[makeQuery(id+"F3.opExtrude","CAP_FACE",FACE,{"disambiguationData":[OSD([sQuery(id+"F2.wireOp",EDGE,"E19"),sQuery(id+"F2.wireOp",EDGE,"E20"),sQuery(id+"F2.wireOp",EDGE,"E21"),sQuery(id+"F2.wireOp",EDGE,"E22"),sQuery(id+"F2.wireOp",EDGE,"E23")])],"isStart":true})]});
            var Q78;
            Q78=makeQuery(id+"F1.opExtrude","CAP_EDGE",EDGE,{"disambiguationData":[OSD([sQuery(id+"F0.wireOp",EDGE,"E13")])],"isStart":false});
            var Q79;
            {var subQ0=sQuery(id+"F0.wireOp",EDGE,"E10");Q79=makeQuery(id+"F7.opFillet","BLEND_EDGE",EDGE,{"blendedFrom":[makeQuery(id+"F1.opExtrude","SWEPT_EDGE",EDGE,{"disambiguationData":[OSD([sQuery(id+"F0.wireOp",EDGE,"E9"),subQ0])]}),makeQuery(id+"F1.opExtrude","SWEPT_FACE",FACE,{"disambiguationData":[OSD([subQ0])]})],"blendedInto":[makeQuery(id+"F1.opExtrude","SWEPT_FACE",FACE,{"disambiguationData":[OSD([subQ0])]})]});}
            var Q80;
            Q80=makeQuery(id+"F1.opExtrude","CAP_EDGE",EDGE,{"disambiguationData":[OSD([sQuery(id+"F0.wireOp",EDGE,"E12")])],"isStart":false});
            var Q81;
            {var subQ0=sQuery(id+"F0.wireOp",EDGE,"E12");Q81=makeQuery(id+"F7.opFillet","BLEND_EDGE",EDGE,{"blendedFrom":[makeQuery(id+"F1.opExtrude","SWEPT_EDGE",EDGE,{"disambiguationData":[OSD([subQ0,sQuery(id+"F0.wireOp",EDGE,"E13")])]}),makeQuery(id+"F1.opExtrude","SWEPT_FACE",FACE,{"disambiguationData":[OSD([subQ0])]})],"blendedInto":[makeQuery(id+"F1.opExtrude","SWEPT_FACE",FACE,{"disambiguationData":[OSD([subQ0])]})]});}
            var Q82;
            Q82=makeQuery(id+"F11.boolean.opBoolean","COPY",EDGE,{"derivedFrom":makeQuery(id+"F11.opExtrude","CAP_EDGE",EDGE,{"disambiguationData":[OSD([sQuery(id+"F10.wireOp",EDGE,"E28")])],"isStart":false})});
            var Q83;
            Q83=makeQuery(id+"F1.opExtrude","CAP_EDGE",EDGE,{"disambiguationData":[OSD([sQuery(id+"F0.wireOp",EDGE,"E12")])],"isStart":true});
            var Q84;
            Q84=makeQuery(id+"F14.boolean.opBoolean","INTERSECT",EDGE,{"derivedFrom":[makeQuery(id+"F3.opExtrude","SWEPT_FACE",FACE,{"disambiguationData":[OSD([sQuery(id+"F2.wireOp",EDGE,"E22")])]}),makeQuery(id+"F14.opExtrude","SWEPT_FACE",FACE,{"disambiguationData":[OSD([sQuery(id+"F13.wireOp",EDGE,"E30.right")])]})]});
            var Q85;
            Q85=makeQuery(id+"F14.boolean.opBoolean","INTERSECT",EDGE,{"derivedFrom":[makeQuery(id+"F3.opExtrude","SWEPT_FACE",FACE,{"disambiguationData":[OSD([sQuery(id+"F2.wireOp",EDGE,"E22")])]}),makeQuery(id+"F14.opExtrude","SWEPT_FACE",FACE,{"disambiguationData":[OSD([sQuery(id+"F13.wireOp",EDGE,"E30.left")])]})]});
            var Q86;
            Q86=makeQuery(id+"F14.boolean.opBoolean","COPY",EDGE,{"derivedFrom":makeQuery(id+"F14.opExtrude","CAP_EDGE",EDGE,{"disambiguationData":[OSD([sQuery(id+"F13.wireOp",EDGE,"E30.right")])],"isStart":true})});
            var Q87;
            Q87=makeQuery(id+"F14.boolean.opBoolean","COPY",EDGE,{"derivedFrom":makeQuery(id+"F14.opExtrude","CAP_EDGE",EDGE,{"disambiguationData":[OSD([sQuery(id+"F13.wireOp",EDGE,"E30.left")])],"isStart":true})});
            var Q88;
            Q88=makeQuery(id+"F15.opFillet","BLEND_EDGE",EDGE,{"blendedFrom":[makeQuery(id+"F14.boolean.opBoolean","COPY",EDGE,{"derivedFrom":makeQuery(id+"F14.opExtrude","SWEPT_EDGE",EDGE,{"disambiguationData":[OSD([sQuery(id+"F13.wireOp",EDGE,"E30.bottom"),sQuery(id+"F13.wireOp",EDGE,"E30.left")])]})}),makeQuery(id+"F3.opExtrude","SWEPT_FACE",FACE,{"disambiguationData":[OSD([sQuery(id+"F2.wireOp",EDGE,"E21")])]})],"blendedInto":[makeQuery(id+"F3.opExtrude","SWEPT_FACE",FACE,{"disambiguationData":[OSD([sQuery(id+"F2.wireOp",EDGE,"E21")])]})]});
            var Q89;
            Q89=makeQuery(id+"F15.opFillet","BLEND_EDGE",EDGE,{"blendedFrom":[makeQuery(id+"F14.boolean.opBoolean","COPY",EDGE,{"derivedFrom":makeQuery(id+"F14.opExtrude","SWEPT_EDGE",EDGE,{"disambiguationData":[OSD([sQuery(id+"F13.wireOp",EDGE,"E30.bottom"),sQuery(id+"F13.wireOp",EDGE,"E30.right")])]})}),makeQuery(id+"F3.opExtrude","SWEPT_FACE",FACE,{"disambiguationData":[OSD([sQuery(id+"F2.wireOp",EDGE,"E21")])]})],"blendedInto":[makeQuery(id+"F3.opExtrude","SWEPT_FACE",FACE,{"disambiguationData":[OSD([sQuery(id+"F2.wireOp",EDGE,"E21")])]})]});
            var Q90;
            Q90=makeQuery(id+"F1.opExtrude","CAP_EDGE",EDGE,{"disambiguationData":[OSD([sQuery(id+"F0.wireOp",EDGE,"E13")])],"isStart":true});
            var Q91;
            Q91=makeQuery(id+"F1.opExtrude","CAP_EDGE",EDGE,{"disambiguationData":[OSD([sQuery(id+"F0.wireOp",EDGE,"E10")])],"isStart":false});
            chamfer(context, id + "F16", {"entities" : qUnion([Q0, Q1, Q2, Q3, Q4, Q5, Q6, Q7, Q8, Q9, Q10, Q11, Q12, Q13, Q14, Q15, Q16, Q17, Q18, Q19, Q20, Q21, Q22, Q23, Q24, Q25, Q26, Q27, Q28, Q29, Q30, Q31, Q32, Q33, Q34, Q35, Q36, Q37, Q38, Q39, Q40, Q41, Q42, Q43, Q44, Q45, Q46, Q47, Q48, Q49, Q50, Q51, Q52, Q53, Q54, Q55, Q56, Q57, Q58, Q59, Q60, Q61, Q62, Q63, Q64, Q65, Q66, Q67, Q68, Q69, Q70, Q71, Q72, Q73, Q74, Q75, Q76, Q77, Q78, Q79, Q80, Q81, Q82, Q83, Q84, Q85, Q86, Q87, Q88, Q89, Q90, Q91]), "width" : 0.25 * mm, "tangentPropagation" : true});
        }
        {
            var Q0;
            {var subQ0=sQuery(id+"F4.wireOp",EDGE,"E26");Q0=makeQuery(id+"F4.imprint","IMPRINT",FACE,{"disambiguationData":[TD([[makeQuery(id+"F4.imprint","IMPRINT",EDGE,{"derivedFrom":subQ0}),1.0]])]});}
            extrude(context, id + "F17", {"entities" : qUnion([Q0]), "operationType" : NewBodyOperationType.REMOVE, "oppositeDirection" : true, "depth" : 12.7 * mm, "offsetDistance" : 25.4 * mm});
        }
        {
            var Q0;
            Q0=makeQuery(id+"F3.opExtrude","SWEPT_FACE",FACE,{"disambiguationData":[OSD([sQuery(id+"F2.wireOp",EDGE,"E22")])]});
            var sketch = newSketch(context, id + "F18", { "sketchPlane" : qUnion([Q0])});
            skLineSegment(sketch, "E31", {"start": v(8.48, -11.17) * mm, "end": v(-1.68, -11.17) * mm});
            skLineSegment(sketch, "E32", {"start": v(8.48, -13.2) * mm, "end": v(-1.68, -13.2) * mm});
            skLineSegment(sketch, "E33", {"start": v(-1.68, -11.17) * mm, "end": v(-1.68, -13.2) * mm});
            skLineSegment(sketch, "E34", {"start": v(8.48, -11.17) * mm, "end": v(9.44, -11.17) * mm});
            skLineSegment(sketch, "E35", {"start": v(9.44, -11.17) * mm, "end": v(9.44, -13.2) * mm});
            skLineSegment(sketch, "E36", {"start": v(9.44, -13.2) * mm, "end": v(8.48, -13.2) * mm});
            skSolve(sketch);
        }
        {
            var Q0;
            Q0 = qSketchRegion(id + "F18", true);
            var Q1;
            Q1=makeQuery(id+"F18.imprint","IMPRINT",FACE,{"disambiguationData":[TD([[makeQuery(id+"F18.imprint","IMPRINT",EDGE,{"derivedFrom":sQuery(id+"F18.wireOp",EDGE,"E31")}),1.0]])]});
            extrude(context, id + "F19", {"entities" : qUnion([Q0, Q1]), "operationType" : NewBodyOperationType.REMOVE, "oppositeDirection" : true, "depth" : 1.9 * mm, "offsetDistance" : 25.4 * mm});
        }
        {
            var Q0;
            Q0=makeQuery(id+"F19.boolean.opBoolean","COPY",EDGE,{"derivedFrom":makeQuery(id+"F19.opExtrude","SWEPT_EDGE",EDGE,{"disambiguationData":[OSD([sQuery(id+"F18.wireOp",EDGE,"E31"),sQuery(id+"F18.wireOp",EDGE,"E33")])]})});
            var Q1;
            Q1=makeQuery(id+"F19.boolean.opBoolean","COPY",EDGE,{"derivedFrom":makeQuery(id+"F19.opExtrude","SWEPT_EDGE",EDGE,{"disambiguationData":[OSD([sQuery(id+"F18.wireOp",EDGE,"E32"),sQuery(id+"F18.wireOp",EDGE,"E33")])]})});
            fillet(context, id + "F20", {"entities" : qUnion([Q0, Q1]), "radius" : 1.02 * mm, "tangentPropagation" : true, "allowEdgeOverflow" : false});
        }
        {
            var Q0;
            Q0=qCreatedBy(makeId("Top.planeOp"),FACE);
            cPlane(context, id + "F21", {"entities" : qUnion([Q0]), "cplaneType" : CPlaneType.OFFSET, "offset" : 19.99 * mm, "oppositeDirection" : true, "width" : 152.4 * mm, "height" : 152.4 * mm});
        }
        {
            var Q0;
            Q0=qCreatedBy(id+"F5.planeOp",FACE);
            var sketch = newSketch(context, id + "F22", { "sketchPlane" : qUnion([Q0])});
            skCircle(sketch, "E37", {"center": v(-19.32, -16.55) * mm, "radius": 1.8 * mm});
            skCircle(sketch, "E38", {"center": v(19.57, -16.55) * mm, "radius": 1.8 * mm});
            skSolve(sketch);
        }
        {
            var Q0;
            Q0 = qSketchRegion(id + "F22", true);
            extrude(context, id + "F23", {"entities" : qUnion([Q0]), "operationType" : NewBodyOperationType.REMOVE, "oppositeDirection" : true, "depth" : 5.7 * mm, "offsetDistance" : 25.4 * mm});
        }
        {
            var Q0;
            Q0=qCreatedBy(id+"F21.planeOp",FACE);
            var sketch = newSketch(context, id + "F24", { "sketchPlane" : qUnion([Q0])});
            skCircle(sketch, "E39", {"center": v(-19.46, -13) * mm, "radius": 2.54 * mm});
            skCircle(sketch, "E40", {"center": v(19.46, -13) * mm, "radius": 2.54 * mm});
            skSolve(sketch);
        }
        {
            var Q0;
            Q0 = qSketchRegion(id + "F24", true);
            extrude(context, id + "F25", {"entities" : qUnion([Q0]), "operationType" : NewBodyOperationType.REMOVE, "depth" : 6.02 * mm, "offsetDistance" : 25.4 * mm});
        }
    });
